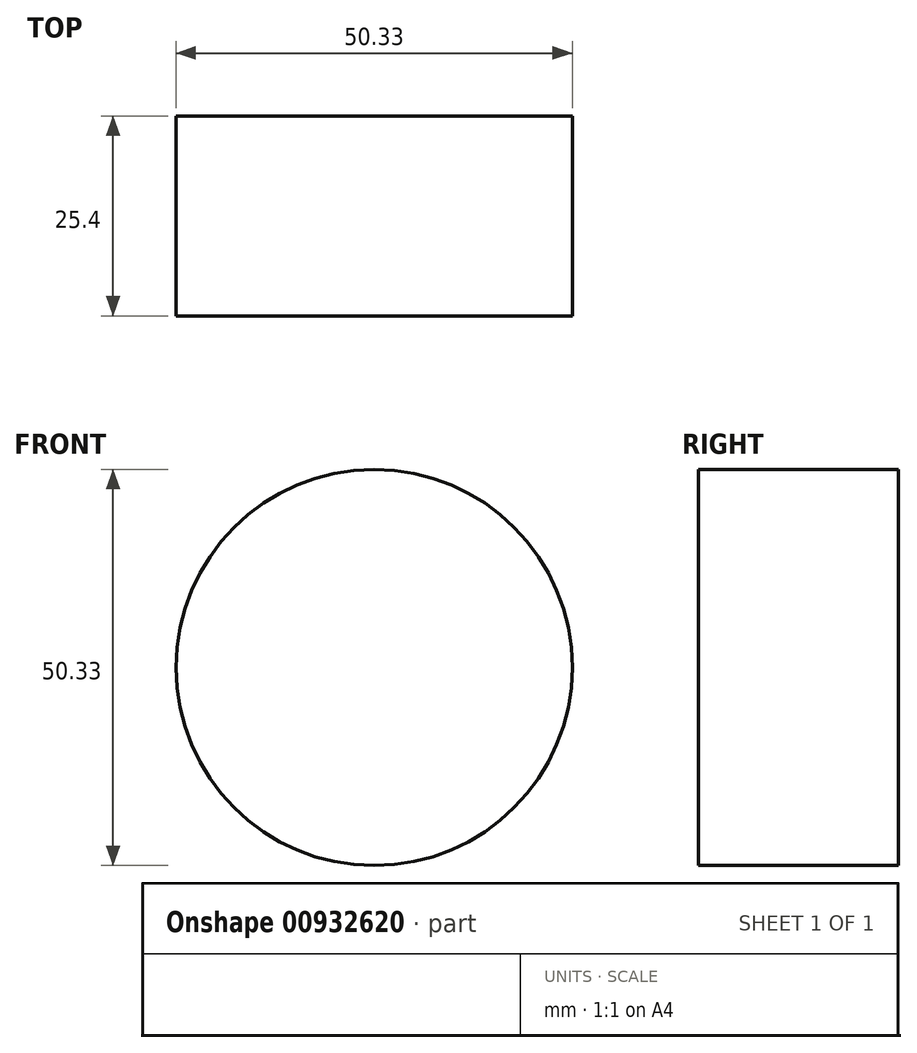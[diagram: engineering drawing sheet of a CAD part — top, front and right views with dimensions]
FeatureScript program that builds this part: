
annotation { "Feature Type Name" : "Feature", "Feature Type Description" : "" }
export const myFeature = defineFeature(function(context is Context, id is Id, definition is map)
    precondition{}
    {
        {
            var Q0;
            Q0=qCreatedBy(makeId("Front.planeOp"),FACE);
            var sketch = newSketch(context, id + "F0", { "sketchPlane" : qUnion([Q0])});
            skCircle(sketch, "E0", {"center": v(-93, 28.92) * mm, "radius": 25.16 * mm});
            skSolve(sketch);
        }
        {
            var Q0;
            Q0 = qSketchRegion(id + "F0", true);
            extrude(context, id + "F1", {"entities" : qUnion([Q0]), "depth" : 25.4 * mm, "offsetDistance" : 25.4 * mm});
        }
    });
